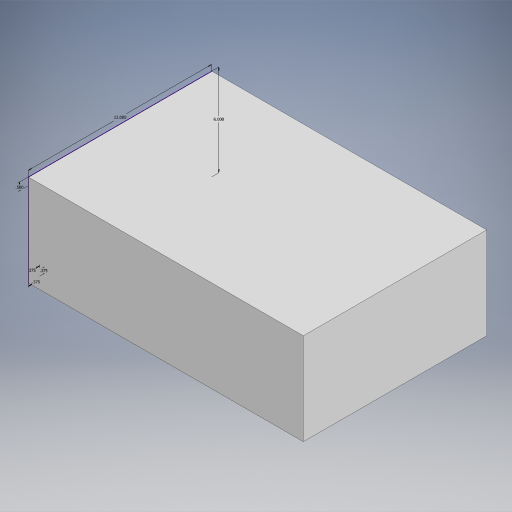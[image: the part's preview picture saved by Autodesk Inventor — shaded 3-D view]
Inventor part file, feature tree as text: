
AUTODESK INVENTOR PART (.ipt)
format: ipt  version: 2023 (Build 270158000, 158)  size: 223,744 bytes
history: native  units: in
note: dims shown in document units (in); Inventor stores cm internally (conversion verified against a paired STEP export)
features: other x5, extrude x3, sketch x1
ambient origin geometry x8: Origin, YZ Plane, XZ Plane, XY Plane, X Axis, Y Axis, Z Axis, Center Point
bodies: Body1 (feature_tree)
feature tree (9):
  other  "Table"
  other  "Typ_rect-01"
  other  "Typ_rect-02"
  other  "Typ_rect-03"
  other  "Typ_rect-04"
  sketch  "Sketch2"  dims[d11=0.0in d12=18.0in d13=0.0in d14=18.0in d15=0.0in]
  extrude  "Main"  Depth=18.0in TaperAngle=0.0deg
  extrude  "Wash"  Depth=18.0in TaperAngle=0.0deg
  extrude  "Drip"  [1 undecoded]
note: 1 required parameter value undecoded (feature->parameter linkage not recoverable at this tier; creation-order binding heuristic only, values carry confidence <= 0.55)
